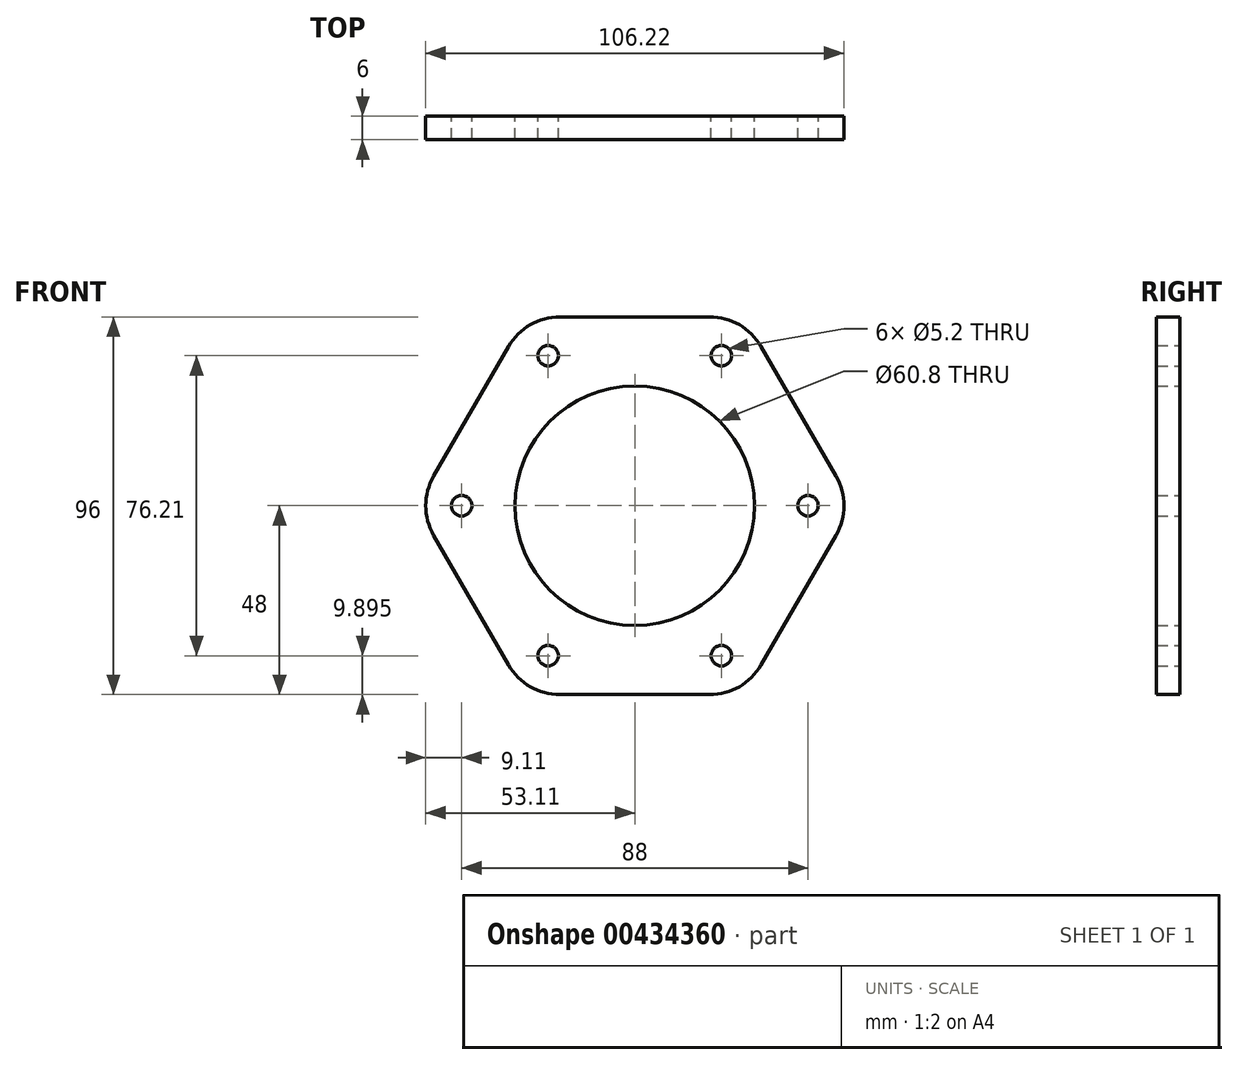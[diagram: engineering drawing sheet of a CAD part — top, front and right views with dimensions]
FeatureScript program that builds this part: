
annotation { "Feature Type Name" : "Feature", "Feature Type Description" : "" }
export const myFeature = defineFeature(function(context is Context, id is Id, definition is map)
    precondition{}
    {
        {
            var Q0;
            Q0=qCreatedBy(makeId("Front.planeOp"),FACE);
            var sketch = newSketch(context, id + "F0", { "sketchPlane" : qUnion([Q0])});
            skCircle(sketch, "E0", {"center": v(0, 0) * mm, "radius": 30.4 * mm});
            skCircle(sketch, "E1.cCircle", {"center": v(0, 0) * mm, "radius": 48 * mm, "construction": true});
            skLineSegment(sketch, "E1.0", {"start": v(-27.71, 48) * mm, "end": v(27.71, 48) * mm});
            skLineSegment(sketch, "E1.1", {"start": v(27.71, 48) * mm, "end": v(55.43, 0) * mm});
            skLineSegment(sketch, "E1.2", {"start": v(55.43, 0) * mm, "end": v(27.71, -48) * mm});
            skLineSegment(sketch, "E1.3", {"start": v(27.71, -48) * mm, "end": v(-27.71, -48) * mm});
            skLineSegment(sketch, "E1.4", {"start": v(-27.71, -48) * mm, "end": v(-55.43, 0) * mm});
            skLineSegment(sketch, "E1.5", {"start": v(-55.43, 0) * mm, "end": v(-27.71, 48) * mm});
            skPoint(sketch, "E1.0.midPoint", {"position": v(0, 48) * mm});
            skCircle(sketch, "E2", {"center": v(0, 0) * mm, "radius": 44 * mm, "construction": true});
            skLineSegment(sketch, "E3", {"start": v(0, 0) * mm, "end": v(27.71, 48) * mm, "construction": true});
            skCircle(sketch, "E4", {"center": v(22, 38.1) * mm, "radius": 2.6 * mm});
            skLineSegment(sketch, "E5.1.0", {"start": v(0, 0) * mm, "end": v(-27.71, 48) * mm, "construction": true});
            skCircle(sketch, "E5.1.1", {"center": v(-22, 38.1) * mm, "radius": 2.6 * mm});
            skLineSegment(sketch, "E5.2.0", {"start": v(0, 0) * mm, "end": v(-55.43, 0) * mm, "construction": true});
            skCircle(sketch, "E5.2.1", {"center": v(-44, 0) * mm, "radius": 2.6 * mm});
            skLineSegment(sketch, "E6.2.3.0", {"start": v(0, 0) * mm, "end": v(-27.71, -48) * mm, "construction": true});
            skCircle(sketch, "E6.3.3.0", {"center": v(-22, -38.1) * mm, "radius": 2.6 * mm});
            skLineSegment(sketch, "E6.2.4.0", {"start": v(0, 0) * mm, "end": v(27.71, -48) * mm, "construction": true});
            skCircle(sketch, "E6.3.4.0", {"center": v(22, -38.1) * mm, "radius": 2.6 * mm});
            skLineSegment(sketch, "E6.2.5.0", {"start": v(0, 0) * mm, "end": v(55.43, 0) * mm, "construction": true});
            skCircle(sketch, "E6.3.5.0", {"center": v(44, 0) * mm, "radius": 2.6 * mm});
            skSolve(sketch);
        }
        {
            var Q0;
            Q0=makeQuery(id+"F0.imprint","IMPRINT",FACE,{"disambiguationData":[TD([[makeQuery(id+"F0.imprint","IMPRINT",EDGE,{"derivedFrom":sQuery(id+"F0.wireOp",EDGE,"E0")}),-1.0]])]});
            var Q1;
            Q1=sQuery(id+"F0.wireOp",EDGE,"E2");
            extrude(context, id + "F1", {"entities" : qUnion([Q0]), "surfaceEntities" : qUnion([Q1]), "depth" : 6 * mm, "offsetDistance" : 25 * mm});
        }
        {
            var Q0;
            Q0=makeQuery(id+"F1.opExtrude","SWEPT_EDGE",EDGE,{"disambiguationData":[OSD([sQuery(id+"F0.wireOp",EDGE,"E1.0"),sQuery(id+"F0.wireOp",EDGE,"E1.5")])]});
            var Q1;
            Q1=makeQuery(id+"F1.opExtrude","SWEPT_EDGE",EDGE,{"disambiguationData":[OSD([sQuery(id+"F0.wireOp",EDGE,"E1.4"),sQuery(id+"F0.wireOp",EDGE,"E1.5")])]});
            var Q2;
            Q2=makeQuery(id+"F1.opExtrude","SWEPT_EDGE",EDGE,{"disambiguationData":[OSD([sQuery(id+"F0.wireOp",EDGE,"E1.3"),sQuery(id+"F0.wireOp",EDGE,"E1.4")])]});
            var Q3;
            Q3=makeQuery(id+"F1.opExtrude","SWEPT_EDGE",EDGE,{"disambiguationData":[OSD([sQuery(id+"F0.wireOp",EDGE,"E1.2"),sQuery(id+"F0.wireOp",EDGE,"E1.3")])]});
            var Q4;
            Q4=makeQuery(id+"F1.opExtrude","SWEPT_EDGE",EDGE,{"disambiguationData":[OSD([sQuery(id+"F0.wireOp",EDGE,"E1.1"),sQuery(id+"F0.wireOp",EDGE,"E1.2")])]});
            var Q5;
            Q5=makeQuery(id+"F1.opExtrude","SWEPT_EDGE",EDGE,{"disambiguationData":[OSD([sQuery(id+"F0.wireOp",EDGE,"E1.0"),sQuery(id+"F0.wireOp",EDGE,"E1.1")])]});
            fillet(context, id + "F2", {"entities" : qUnion([Q0, Q1, Q2, Q3, Q4, Q5]), "radius" : 15 * mm, "tangentPropagation" : true, "allowEdgeOverflow" : false});
        }
    });
